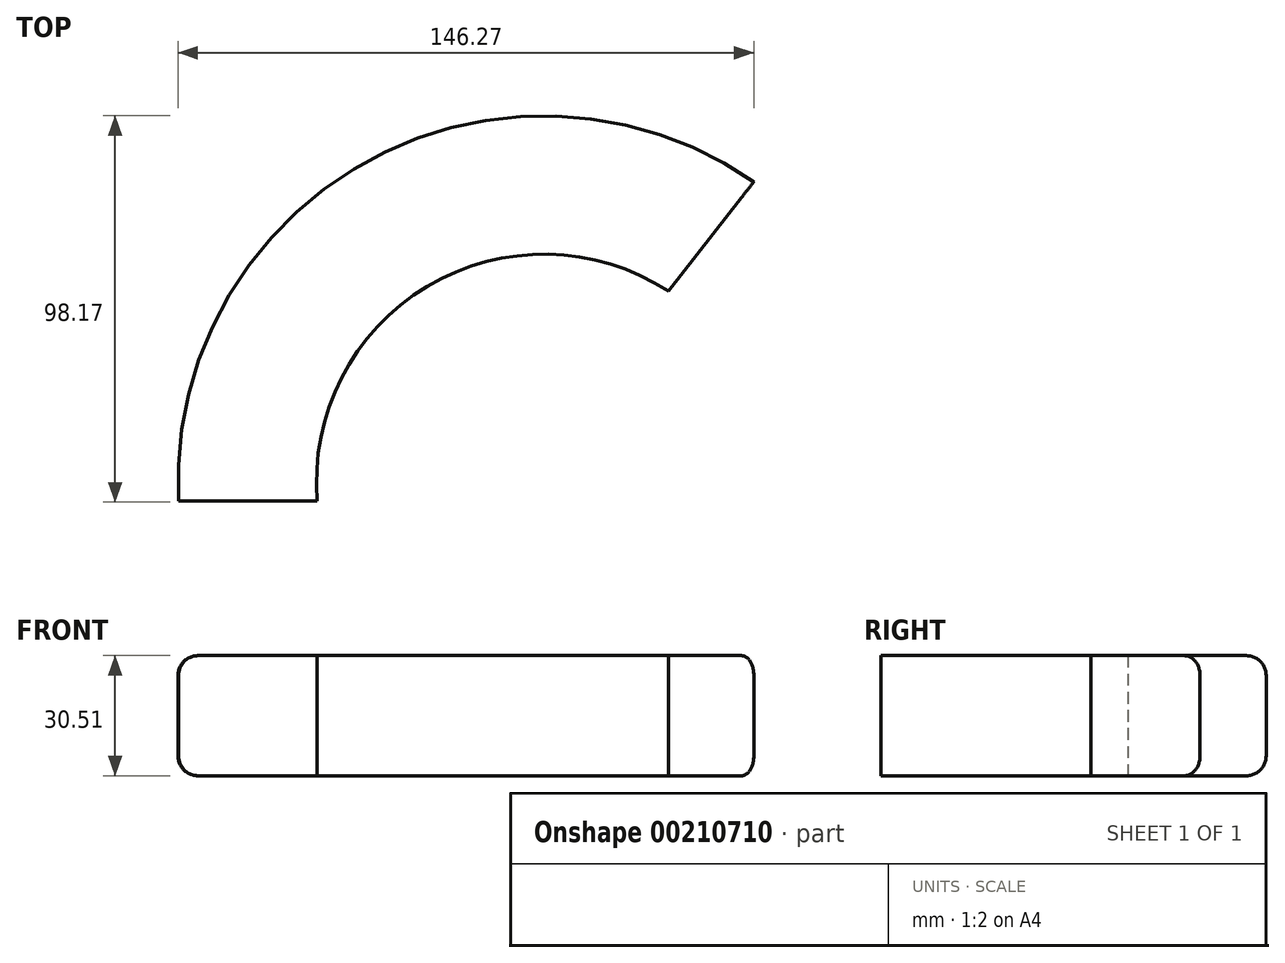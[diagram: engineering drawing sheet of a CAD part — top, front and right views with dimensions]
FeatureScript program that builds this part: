
annotation { "Feature Type Name" : "Feature", "Feature Type Description" : "" }
export const myFeature = defineFeature(function(context is Context, id is Id, definition is map)
    precondition{}
    {
        {
            var Q0;
            Q0=qCreatedBy(makeId("Front.planeOp"),FACE);
            var sketch = newSketch(context, id + "F0", { "sketchPlane" : qUnion([Q0])});
            skLineSegment(sketch, "E0.bottom", {"start": v(-49.76, 0) * mm, "end": v(-19.51, 0) * mm});
            skLineSegment(sketch, "E0.top", {"start": v(-49.76, -30.5) * mm, "end": v(-19.51, -30.5) * mm});
            skLineSegment(sketch, "E0.left", {"start": v(-54.76, -5) * mm, "end": v(-54.76, -25.5) * mm});
            skLineSegment(sketch, "E0.right", {"start": v(-19.51, 0) * mm, "end": v(-19.51, -30.5) * mm});
            skPoint(sketch, "E0.middle", {"position": v(-37.14, -15.25) * mm});
            skPoint(sketch, "E1.visualSharp", {"position": v(-54.76, -30.5) * mm});
            skArc(sketch, "E1.filletArc", {"start": v(-54.76, -25.5) * mm, "mid": v(-53.3, -29.04) * mm, "end": v(-49.76, -30.5) * mm});
            skPoint(sketch, "E2.visualSharp", {"position": v(-54.76, 0) * mm});
            skArc(sketch, "E2.filletArc", {"start": v(-49.76, 0) * mm, "mid": v(-53.3, -1.46) * mm, "end": v(-54.76, -5) * mm});
            skSolve(sketch);
        }
        {
            var Q0;
            Q0=qCreatedBy(makeId("Top.planeOp"),FACE);
            var sketch = newSketch(context, id + "F1", { "sketchPlane" : qUnion([Q0])});
            skArc(sketch, "E3", {"start": v(69.7, 53.37) * mm, "mid": v(8.39, 54.59) * mm, "end": v(-19.58, 0) * mm});
            skSolve(sketch);
        }
        {
            var Q0;
            Q0=makeQuery(id+"F0.imprint","IMPRINT",FACE,{"disambiguationData":[TD([[makeQuery(id+"F0.imprint","IMPRINT",EDGE,{"derivedFrom":sQuery(id+"F0.wireOp",EDGE,"E0.bottom")}),-1.0]])]});
            var Q1;
            Q1=sQuery(id+"F1.wireOp",EDGE,"E3");
            sweep(context, id + "F2", {"profiles" : qUnion([Q0]), "path" : qUnion([Q1])});
        }
    });
